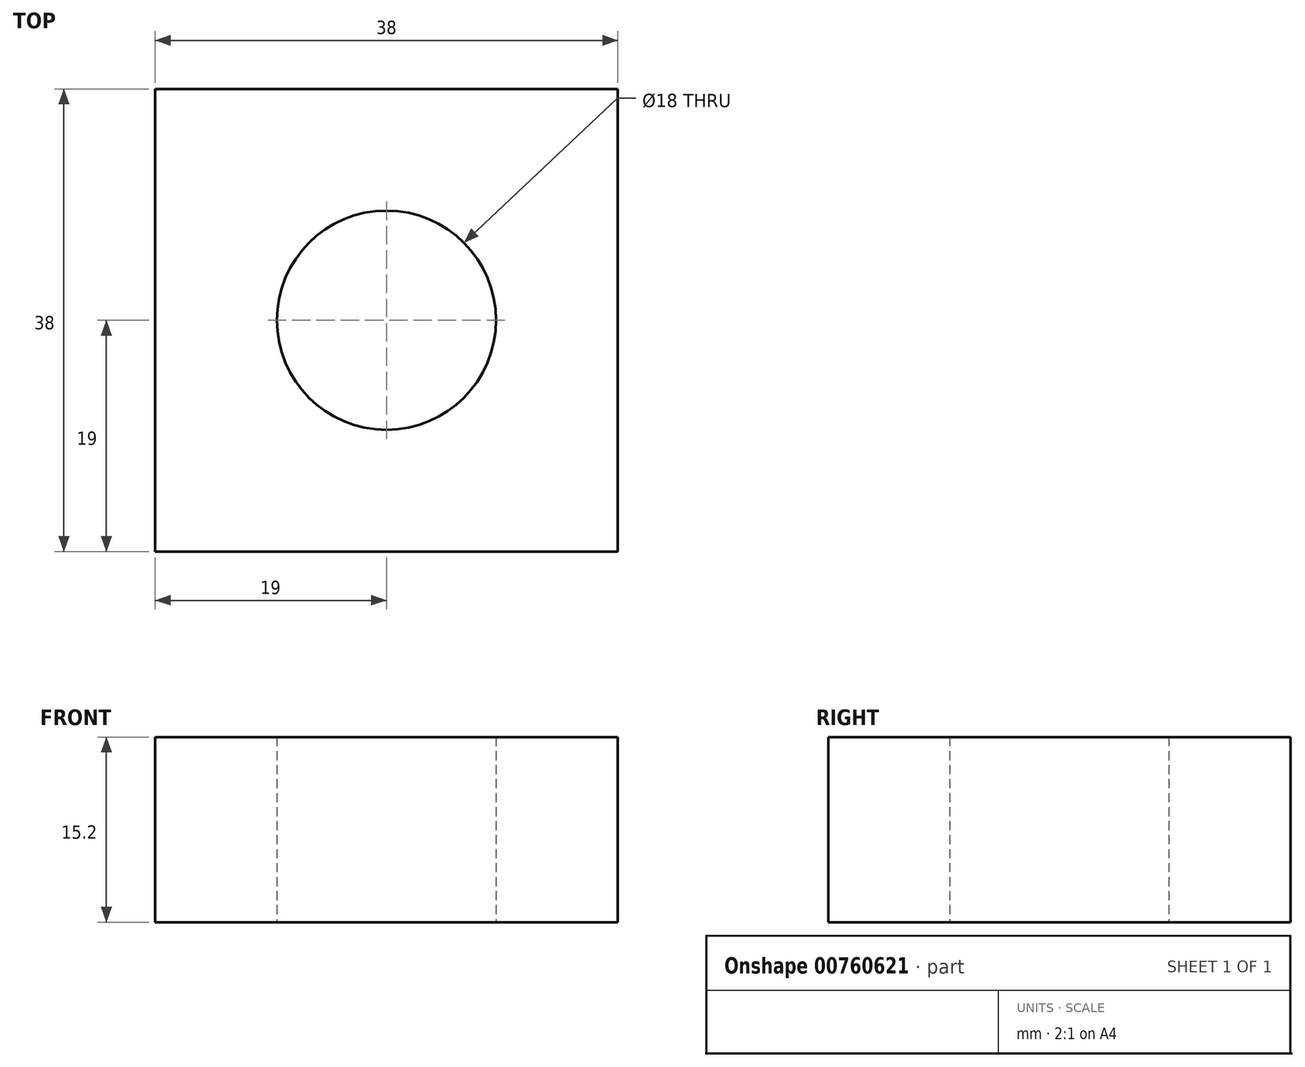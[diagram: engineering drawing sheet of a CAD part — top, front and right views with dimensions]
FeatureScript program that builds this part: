
annotation { "Feature Type Name" : "Feature", "Feature Type Description" : "" }
export const myFeature = defineFeature(function(context is Context, id is Id, definition is map)
    precondition{}
    {
        {
            var Q0;
            Q0=qCreatedBy(makeId("Top.planeOp"),FACE);
            var sketch = newSketch(context, id + "F0", { "sketchPlane" : qUnion([Q0])});
            skCircle(sketch, "E0", {"center": v(0, 0) * mm, "radius": 9 * mm});
            skLineSegment(sketch, "E1.bottom", {"start": v(-19, 19) * mm, "end": v(19, 19) * mm});
            skLineSegment(sketch, "E1.top", {"start": v(-19, -19) * mm, "end": v(19, -19) * mm});
            skLineSegment(sketch, "E1.left", {"start": v(-19, 19) * mm, "end": v(-19, -19) * mm});
            skLineSegment(sketch, "E1.right", {"start": v(19, 19) * mm, "end": v(19, -19) * mm});
            skSolve(sketch);
        }
        {
            var Q0;
            Q0 = qSketchRegion(id + "F0", true);
            extrude(context, id + "F1", {"entities" : qUnion([Q0]), "depth" : 15.2 * mm, "offsetDistance" : 25 * mm});
        }
    });
